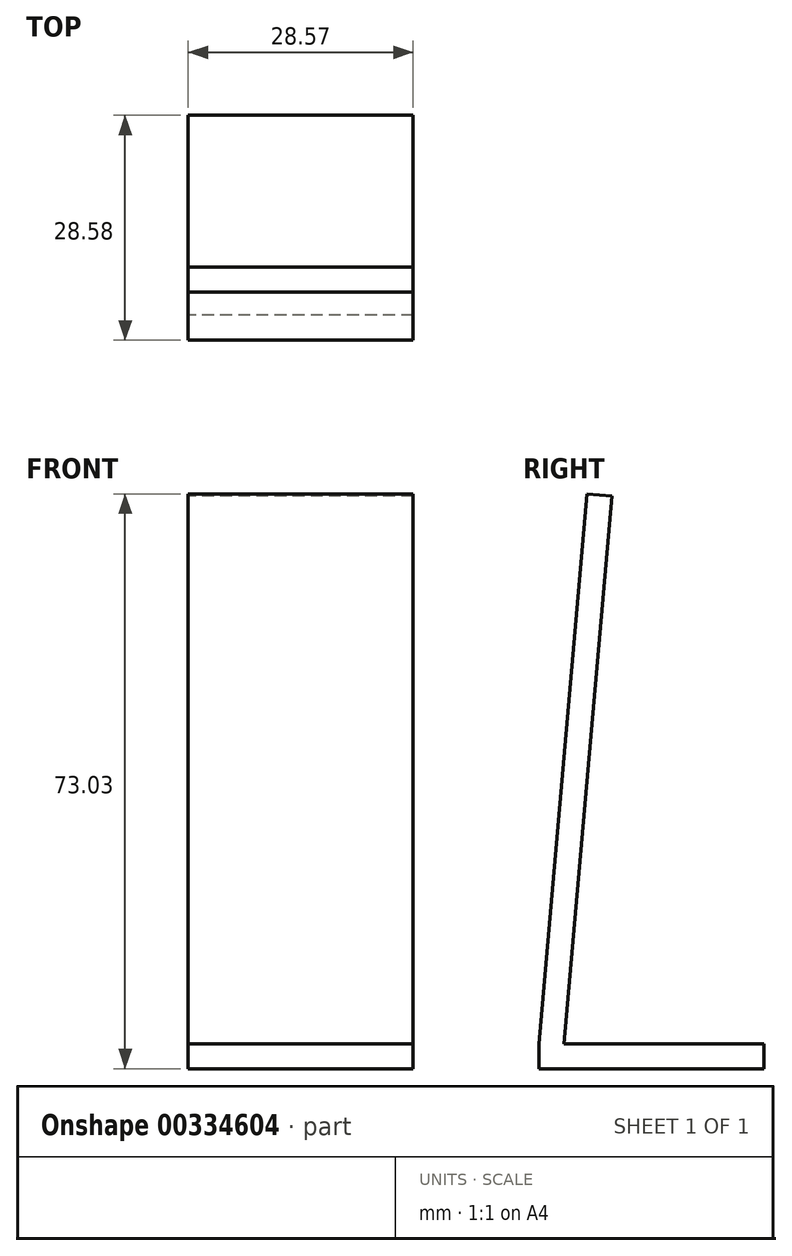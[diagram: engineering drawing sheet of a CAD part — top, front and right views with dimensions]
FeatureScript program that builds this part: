
annotation { "Feature Type Name" : "Feature", "Feature Type Description" : "" }
export const myFeature = defineFeature(function(context is Context, id is Id, definition is map)
    precondition{}
    {
        {
            var Q0;
            Q0=qCreatedBy(makeId("Right.planeOp"),FACE);
            var sketch = newSketch(context, id + "F0", { "sketchPlane" : qUnion([Q0])});
            skLineSegment(sketch, "E0", {"start": v(-14.29, 0) * mm, "end": v(14.29, 0) * mm});
            skLineSegment(sketch, "E1", {"start": v(14.29, 0) * mm, "end": v(14.29, 3.17) * mm});
            skLineSegment(sketch, "E2", {"start": v(14.29, 3.17) * mm, "end": v(-14.29, 3.17) * mm});
            skLineSegment(sketch, "E3", {"start": v(-14.29, 3.17) * mm, "end": v(-14.29, 0) * mm});
            skLineSegment(sketch, "E4", {"start": v(-5.01, 3.17) * mm, "end": v(-5.01, 73.03) * mm, "construction": true});
            skLineSegment(sketch, "E5", {"start": v(-14.29, 3.18) * mm, "end": v(-8.18, 73.03) * mm});
            skLineSegment(sketch, "E6", {"start": v(-8.18, 73.03) * mm, "end": v(-5.01, 72.75) * mm});
            skLineSegment(sketch, "E7", {"start": v(-5.01, 72.75) * mm, "end": v(-11.1, 3.18) * mm});
            skLineSegment(sketch, "E8", {"start": v(-11.1, 3.17) * mm, "end": v(-14.29, 3.17) * mm});
            skSolve(sketch);
        }
        {
            var Q0;
            Q0=qSketchRegion(id+"F0",true);
            extrude(context, id + "F1", {"entities" : qUnion([Q0]), "depth" : 28.57 * mm});
        }
    });
